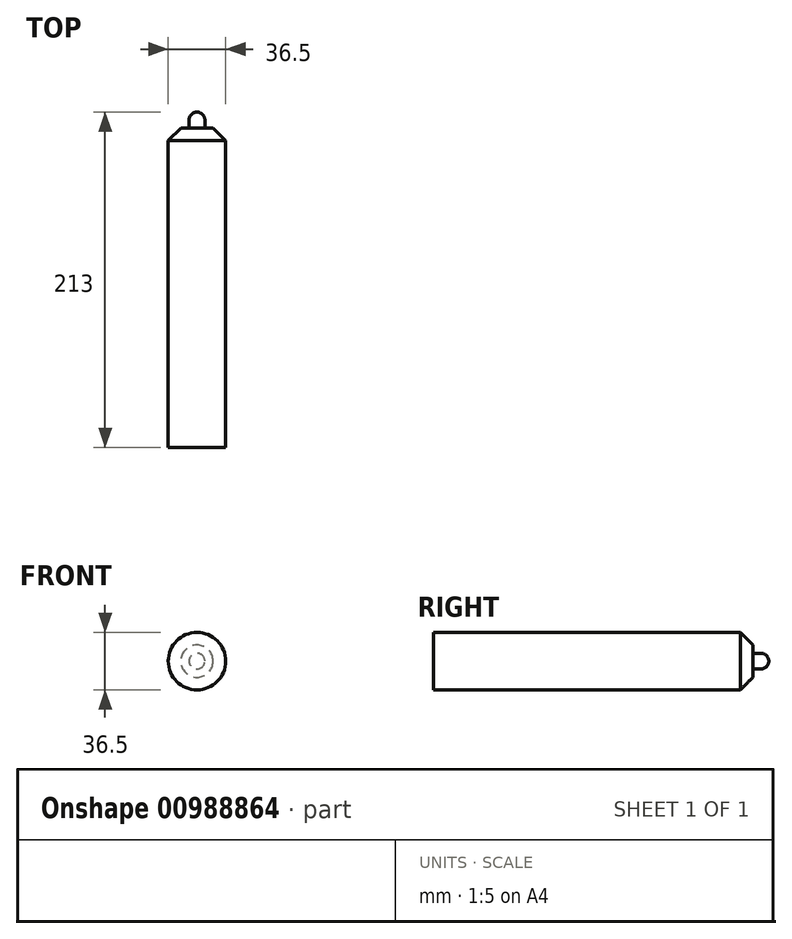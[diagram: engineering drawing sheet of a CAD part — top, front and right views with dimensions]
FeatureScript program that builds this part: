
annotation { "Feature Type Name" : "Feature", "Feature Type Description" : "" }
export const myFeature = defineFeature(function(context is Context, id is Id, definition is map)
    precondition{}
    {
        {
            var Q0;
            Q0=qCreatedBy(makeId("Front.planeOp"),FACE);
            var sketch = newSketch(context, id + "F0", { "sketchPlane" : qUnion([Q0])});
            skCircle(sketch, "E0", {"center": v(0, 0) * mm, "radius": 18.25 * mm});
            skSolve(sketch);
        }
        {
            var Q0;
            Q0 = qSketchRegion(id + "F0", true);
            extrude(context, id + "F1", {"entities" : qUnion([Q0]), "depth" : 203 * mm, "offsetDistance" : 25 * mm});
        }
        {
            var Q0;
            Q0=qCreatedBy(makeId("Front.planeOp"),FACE);
            var sketch = newSketch(context, id + "F2", { "sketchPlane" : qUnion([Q0])});
            skCircle(sketch, "E1", {"center": v(0, 0) * mm, "radius": 5 * mm});
            skSolve(sketch);
        }
        {
            var Q0;
            Q0 = qSketchRegion(id + "F2", true);
            extrude(context, id + "F3", {"entities" : qUnion([Q0]), "operationType" : NewBodyOperationType.ADD, "oppositeDirection" : true, "depth" : 10 * mm, "offsetDistance" : 25 * mm});
        }
        {
            var Q0;
            Q0=makeQuery(id+"F3.opExtrude","CAP_EDGE",EDGE,{"disambiguationData":[OSD([sQuery(id+"F2.wireOp",EDGE,"E1")])],"isStart":false});
            fillet(context, id + "F4", {"entities" : qUnion([Q0]), "radius" : 5 * mm, "allowEdgeOverflow" : false});
        }
        {
            var Q0;
            Q0=makeQuery(id+"F1.opExtrude","CAP_EDGE",EDGE,{"disambiguationData":[OSD([sQuery(id+"F0.wireOp",EDGE,"E0")])],"isStart":true});
            chamfer(context, id + "F5", {"entities" : qUnion([Q0]), "width" : 8 * mm, "tangentPropagation" : true});
        }
    });
